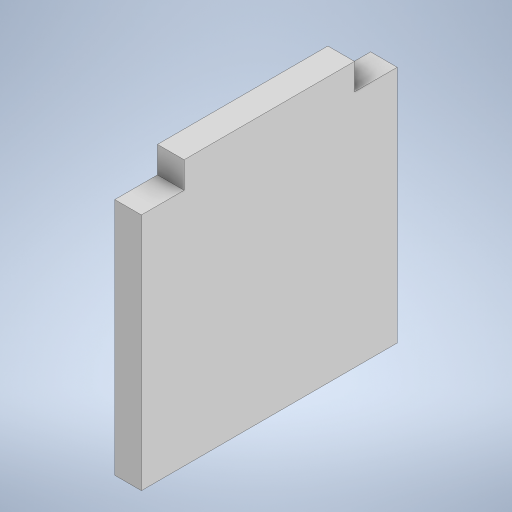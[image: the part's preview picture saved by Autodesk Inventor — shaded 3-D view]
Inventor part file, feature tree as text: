
AUTODESK INVENTOR PART (.ipt)
format: ipt  version: 2024 (Build 280153000, 153)  size: 520,192 bytes
history: native  units: mm
features: extrude x3, sketch x3
ambient origin geometry x8: Origin, YZ Plane, XZ Plane, XY Plane, X Axis, Y Axis, Z Axis, Center Point
bodies: Solid1 (feature_tree)
feature tree (6):
  extrude  "Extrusion1"  Depth=30.0mm
  extrude  "Extrusion2"  Depth=3.125mm
  extrude  "Extrusion3"  Depth=3.1mm TaperAngle=0.0deg
  sketch  "Sketch1"  dims[d0=3.125mm d1=30.0mm]
  sketch  "Sketch3"  dims[d2=17.0mm d3=0.0mm d4=3.125mm]
  sketch  "Sketch4"  dims[d5=19.98mm d6=3.1mm d7=0.0mm d8=11.0mm d9=0.0mm]
